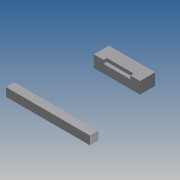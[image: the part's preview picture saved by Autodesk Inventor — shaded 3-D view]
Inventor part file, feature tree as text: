
AUTODESK INVENTOR PART (.ipt)
format: ipt  version: 2015 (Build 190159000, 159)  size: 108,032 bytes
history: native  units: mm
features: extrude x2, sketch x1
ambient origin geometry x8: Origin, YZ Plane, XZ Plane, XY Plane, X Axis, Y Axis, Z Axis, Center Point
bodies: Body1 (feature_tree)
feature tree (3):
  sketch  "Skizze3"  dims[d4=1000.0mm d5=1000.0mm d6=100.0mm d7=550.0mm d8=180.0mm d9=100.0mm d10=100.0mm d11=320.0mm d12=300.0mm d13=350.0mm d14=230.0mm d15=60.0mm d16=-60.0mm d17=130.0mm d18=190.0mm d19=50.0mm d21=283.537414mm d22=40.0mm d23=140.0mm d24=899.502025mm d25=919.104612mm d26=330.793649mm d27=100.0mm d28=0.0mm d29=40.0mm d30=0.0mm]
  extrude  "Extrusion2"  Depth=1000.0mm
  extrude  "Extrusion3"  Depth=100.0mm
